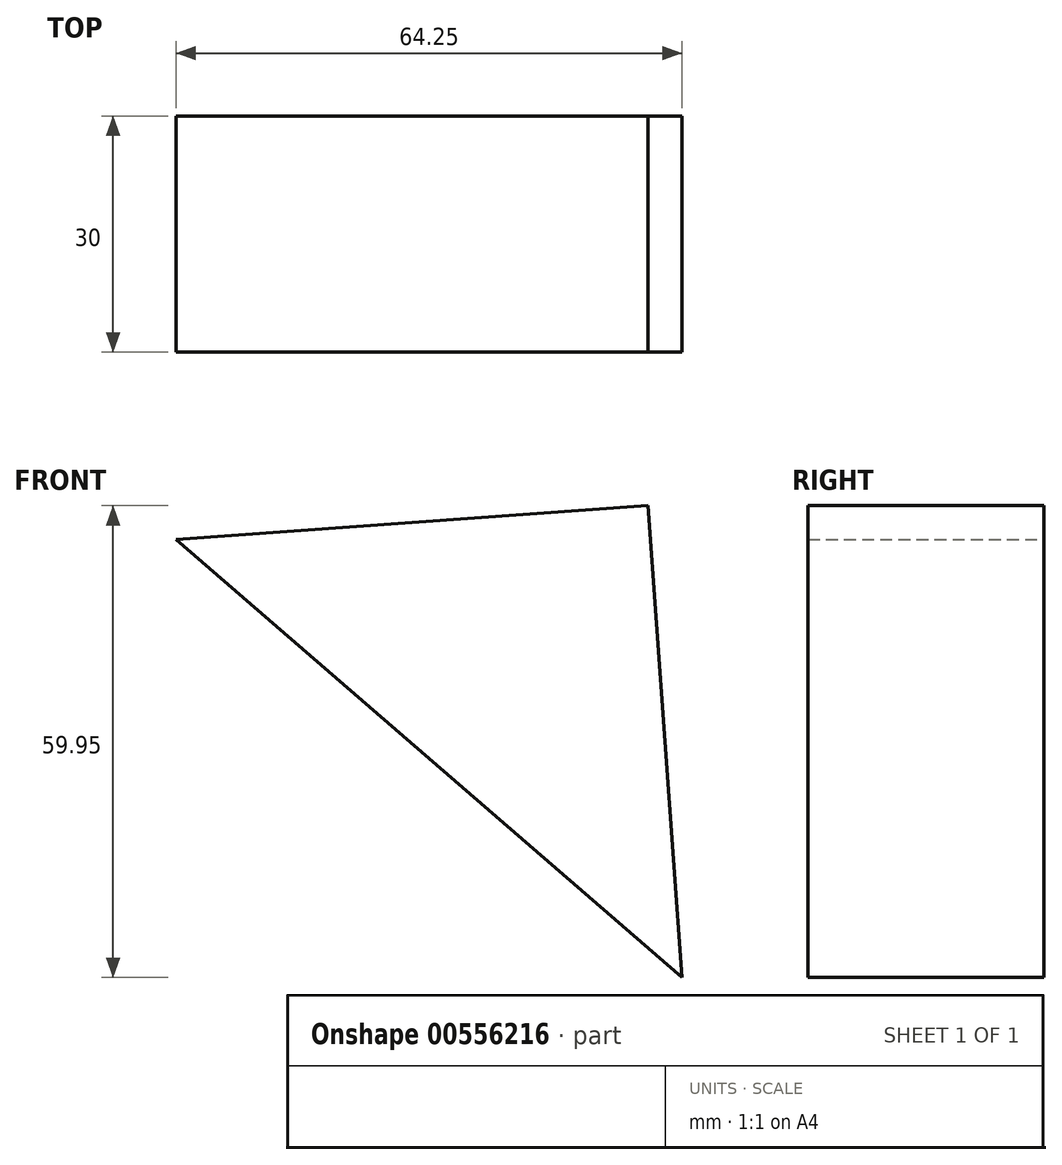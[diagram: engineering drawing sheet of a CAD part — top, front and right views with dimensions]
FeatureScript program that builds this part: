
annotation { "Feature Type Name" : "Feature", "Feature Type Description" : "" }
export const myFeature = defineFeature(function(context is Context, id is Id, definition is map)
    precondition{}
    {
        {
            var Q0;
            Q0=qCreatedBy(makeId("Front.planeOp"),FACE);
            var sketch = newSketch(context, id + "F0", { "sketchPlane" : qUnion([Q0])});
            skLineSegment(sketch, "E0", {"start": v(0, 0) * mm, "end": v(64.25, -55.65) * mm});
            skLineSegment(sketch, "E1", {"start": v(64.25, -55.65) * mm, "end": v(59.95, 4.3) * mm});
            skLineSegment(sketch, "E2", {"start": v(59.95, 4.3) * mm, "end": v(0, 0) * mm});
            skSolve(sketch);
        }
        {
            var Q0;
            Q0 = qSketchRegion(id + "F0", true);
            extrude(context, id + "F1", {"entities" : qUnion([Q0]), "depth" : 30 * mm, "offsetDistance" : 25 * mm});
        }
    });
